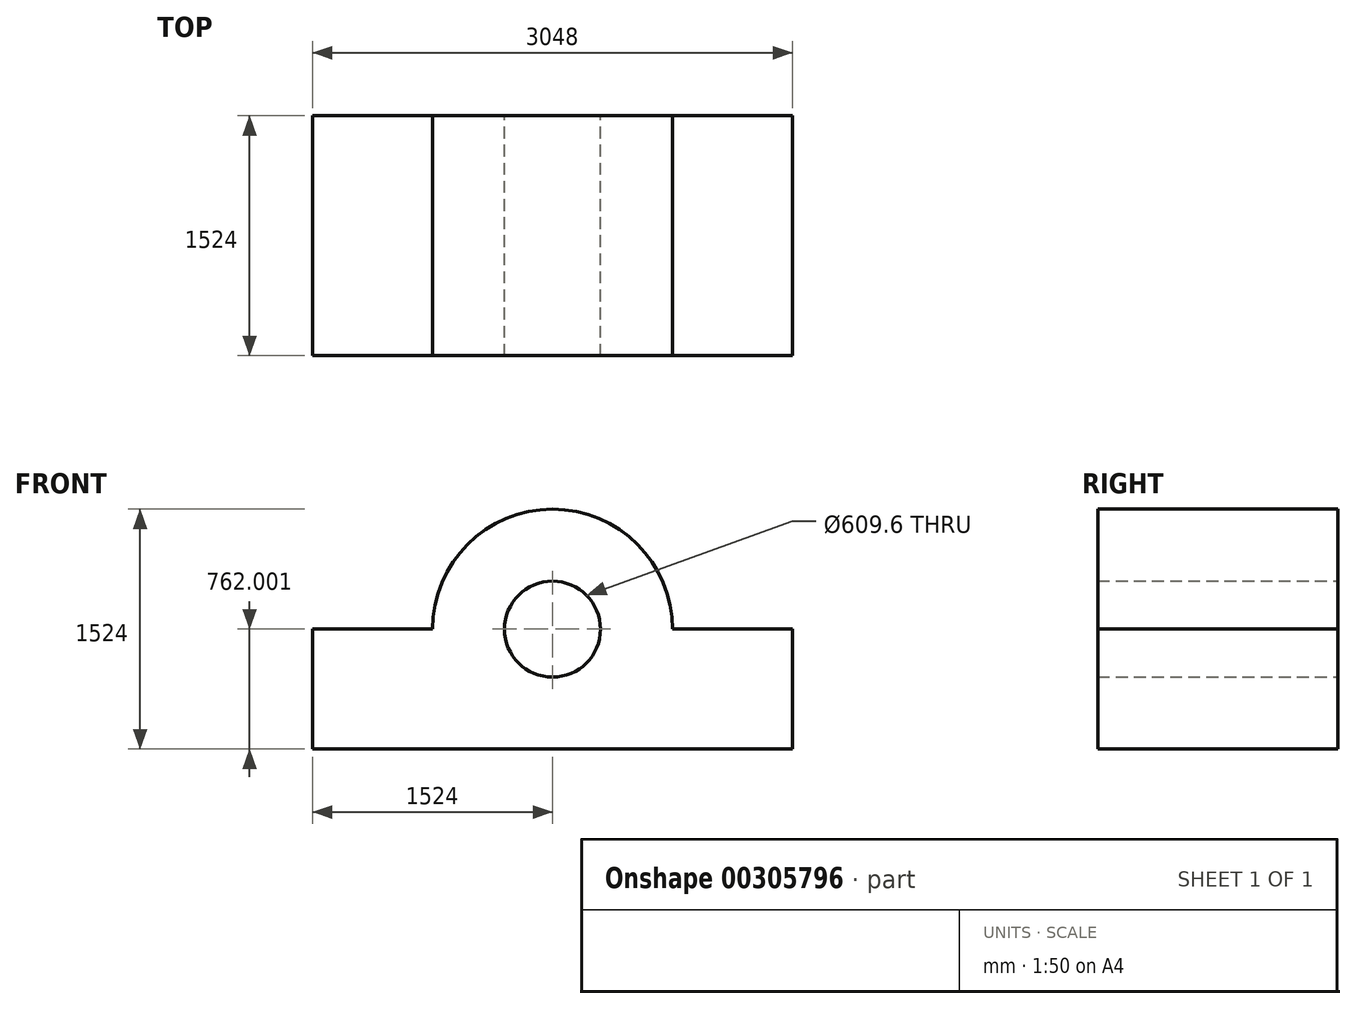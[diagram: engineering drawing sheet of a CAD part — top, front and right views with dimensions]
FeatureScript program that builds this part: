
annotation { "Feature Type Name" : "Feature", "Feature Type Description" : "" }
export const myFeature = defineFeature(function(context is Context, id is Id, definition is map)
    precondition{}
    {
        {
            var Q0;
            Q0=qCreatedBy(makeId("Front.planeOp"),FACE);
            var sketch = newSketch(context, id + "F0", { "sketchPlane" : qUnion([Q0])});
            skLineSegment(sketch, "E0", {"start": v(-1920.58, 457.46) * mm, "end": v(-1920.58, -304.54) * mm});
            skLineSegment(sketch, "E1", {"start": v(-1920.58, -304.54) * mm, "end": v(1127.42, -304.54) * mm});
            skLineSegment(sketch, "E2", {"start": v(1127.42, -304.54) * mm, "end": v(1127.42, 457.46) * mm});
            skLineSegment(sketch, "E3", {"start": v(1127.42, 457.46) * mm, "end": v(365.42, 457.46) * mm});
            skLineSegment(sketch, "E4", {"start": v(-1920.58, 457.46) * mm, "end": v(-1158.58, 457.46) * mm});
            skArc(sketch, "E5", {"start": v(365.42, 457.46) * mm, "mid": v(-396.58, 1219.46) * mm, "end": v(-1158.58, 457.46) * mm});
            skCircle(sketch, "E6", {"center": v(-396.58, 457.46) * mm, "radius": 304.8 * mm});
            skSolve(sketch);
        }
        {
            var Q0;
            Q0=makeQuery(id+"F0.imprint","IMPRINT",FACE,{"disambiguationData":[TD([[makeQuery(id+"F0.imprint","IMPRINT",EDGE,{"derivedFrom":sQuery(id+"F0.wireOp",EDGE,"E0")}),1.0]])]});
            extrude(context, id + "F1", {"entities" : qUnion([Q0]), "depth" : 1524 * mm, "symmetric" : true});
        }
    });
